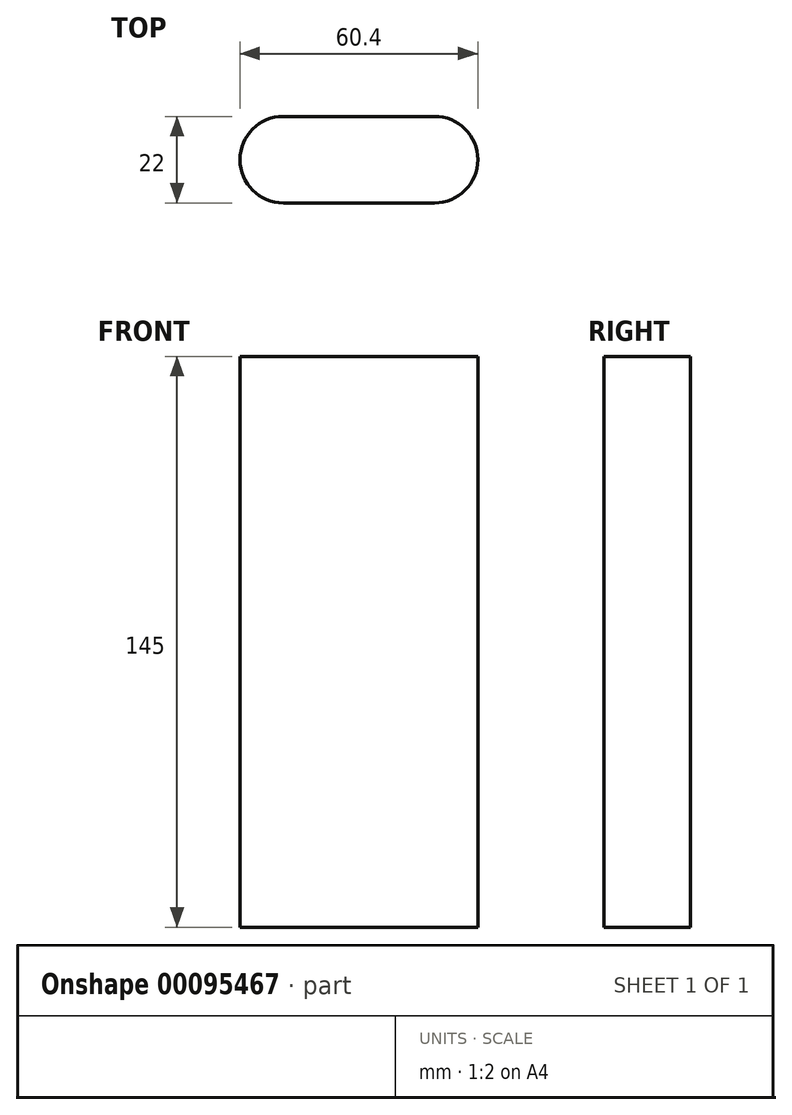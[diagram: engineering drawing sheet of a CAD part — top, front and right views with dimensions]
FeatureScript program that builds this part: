
annotation { "Feature Type Name" : "Feature", "Feature Type Description" : "" }
export const myFeature = defineFeature(function(context is Context, id is Id, definition is map)
    precondition{}
    {
        {
            var Q0;
            Q0=qCreatedBy(makeId("Top.planeOp"),FACE);
            var sketch = newSketch(context, id + "F0", { "sketchPlane" : qUnion([Q0])});
            skLineSegment(sketch, "E0.bottom", {"start": v(-19.2, 11) * mm, "end": v(19.2, 11) * mm});
            skLineSegment(sketch, "E0.top", {"start": v(-19.2, -11) * mm, "end": v(19.2, -11) * mm});
            skLineSegment(sketch, "E0.left", {"start": v(-19.2, 11) * mm, "end": v(-19.2, -11) * mm});
            skLineSegment(sketch, "E0.right", {"start": v(19.2, 11) * mm, "end": v(19.2, -11) * mm});
            skPoint(sketch, "E0.middle", {"position": v(0, 0) * mm});
            skArc(sketch, "E1", {"start": v(-19.2, 11) * mm, "mid": v(-30.2, 0) * mm, "end": v(-19.2, -11) * mm});
            skArc(sketch, "E2", {"start": v(19.2, 11) * mm, "mid": v(30.2, 0) * mm, "end": v(19.2, -11) * mm});
            skSolve(sketch);
        }
        {
            var Q0;
            Q0 = qSketchRegion(id + "F0", true);
            extrude(context, id + "F1", {"entities" : qUnion([Q0]), "endBound" : BoundingType.SYMMETRIC, "depth" : 145 * mm});
        }
    });
